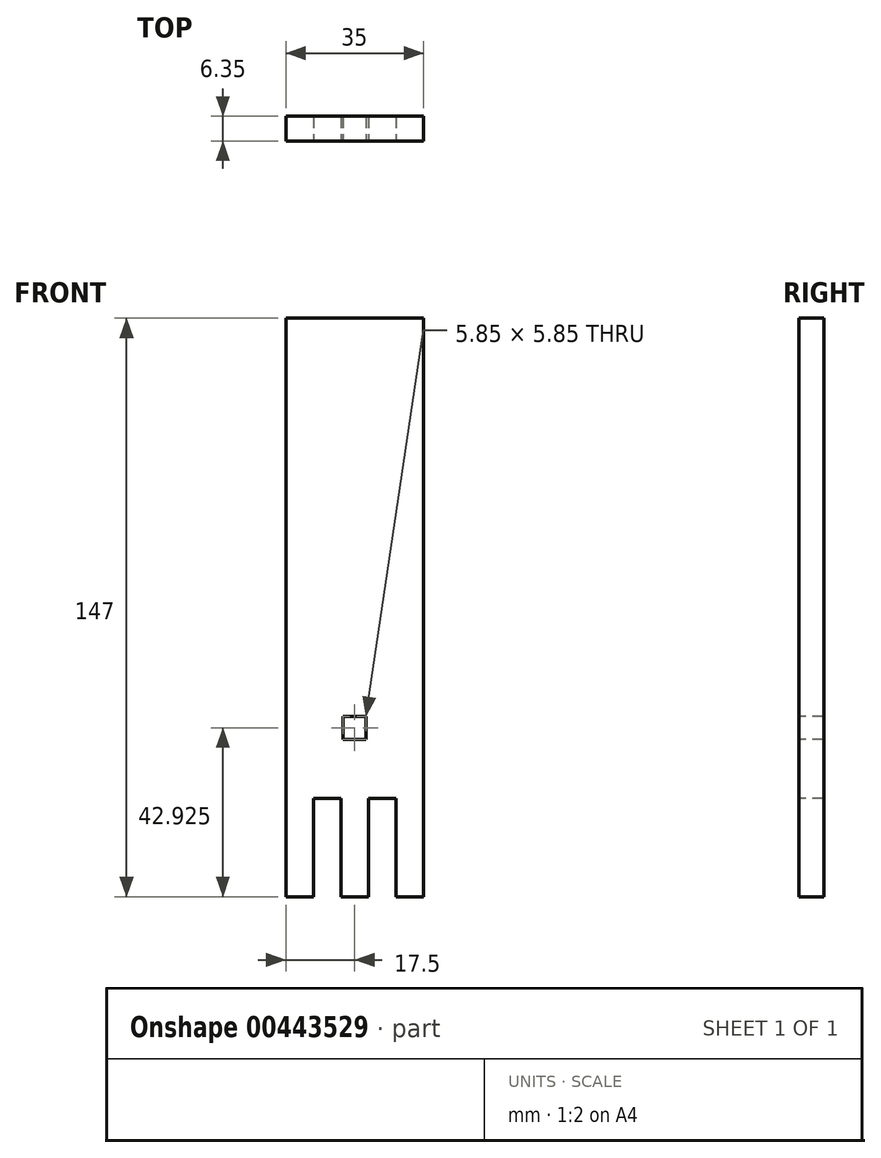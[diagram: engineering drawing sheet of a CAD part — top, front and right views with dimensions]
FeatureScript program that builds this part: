
annotation { "Feature Type Name" : "Feature", "Feature Type Description" : "" }
export const myFeature = defineFeature(function(context is Context, id is Id, definition is map)
    precondition{}
    {
        {
            var Q0;
            Q0=qCreatedBy(makeId("Front.planeOp"),FACE);
            var sketch = newSketch(context, id + "F0", { "sketchPlane" : qUnion([Q0])});
            skLineSegment(sketch, "E0.bottom", {"start": v(0, 0) * mm, "end": v(35, 0) * mm});
            skLineSegment(sketch, "E0.top", {"start": v(0, 122) * mm, "end": v(35, 122) * mm});
            skLineSegment(sketch, "E0.left", {"start": v(0, 0) * mm, "end": v(0, 122) * mm});
            skLineSegment(sketch, "E0.right", {"start": v(35, 0) * mm, "end": v(35, 122) * mm});
            skSolve(sketch);
        }
        {
            var Q0;
            Q0 = qSketchRegion(id + "F0", true);
            extrude(context, id + "F1", {"entities" : qUnion([Q0]), "depth" : 6.35 * mm});
        }
        {
            var Q0;
            Q0=makeQuery(id+"F1.opExtrude","CAP_FACE",FACE,{"disambiguationData":[OSD([sQuery(id+"F0.wireOp",EDGE,"E0.bottom"),sQuery(id+"F0.wireOp",EDGE,"E0.top"),sQuery(id+"F0.wireOp",EDGE,"E0.left"),sQuery(id+"F0.wireOp",EDGE,"E0.right")])],"isStart":false});
            var sketch = newSketch(context, id + "F2", { "sketchPlane" : qUnion([Q0])});
            skLineSegment(sketch, "E1.bottom", {"start": v(0, 0) * mm, "end": v(7, 0) * mm});
            skLineSegment(sketch, "E1.top", {"start": v(0, -25) * mm, "end": v(7, -25) * mm});
            skLineSegment(sketch, "E1.left", {"start": v(0, 0) * mm, "end": v(0, -25) * mm});
            skLineSegment(sketch, "E1.right", {"start": v(7, 0) * mm, "end": v(7, -25) * mm});
            skLineSegment(sketch, "E2.bottom", {"start": v(28, 0) * mm, "end": v(35, 0) * mm});
            skLineSegment(sketch, "E2.top", {"start": v(28, -25) * mm, "end": v(35, -25) * mm});
            skLineSegment(sketch, "E2.left", {"start": v(28, 0) * mm, "end": v(28, -25) * mm});
            skLineSegment(sketch, "E2.right", {"start": v(35, 0) * mm, "end": v(35, -25) * mm});
            skLineSegment(sketch, "E3.bottom", {"start": v(14, 0) * mm, "end": v(21, 0) * mm});
            skLineSegment(sketch, "E3.top", {"start": v(14, -25) * mm, "end": v(21, -25) * mm});
            skLineSegment(sketch, "E3.left", {"start": v(14, 0) * mm, "end": v(14, -25) * mm});
            skLineSegment(sketch, "E3.right", {"start": v(21, 0) * mm, "end": v(21, -25) * mm});
            skSolve(sketch);
        }
        {
            var Q0;
            Q0 = qSketchRegion(id + "F2", true);
            extrude(context, id + "F3", {"entities" : qUnion([Q0]), "operationType" : NewBodyOperationType.ADD, "oppositeDirection" : true, "depth" : 6.35 * mm});
        }
        {
            var Q0;
            Q0=makeQuery(id+"F1.opExtrude","CAP_FACE",FACE,{"disambiguationData":[OSD([sQuery(id+"F0.wireOp",EDGE,"E0.bottom"),sQuery(id+"F0.wireOp",EDGE,"E0.top"),sQuery(id+"F0.wireOp",EDGE,"E0.left"),sQuery(id+"F0.wireOp",EDGE,"E0.right")])],"isStart":false});
            var sketch = newSketch(context, id + "F4", { "sketchPlane" : qUnion([Q0])});
            skLineSegment(sketch, "E4.bottom", {"start": v(14.58, 20.85) * mm, "end": v(20.43, 20.85) * mm});
            skLineSegment(sketch, "E4.top", {"start": v(14.58, 15) * mm, "end": v(20.43, 15) * mm});
            skLineSegment(sketch, "E4.left", {"start": v(14.58, 20.85) * mm, "end": v(14.58, 15) * mm});
            skLineSegment(sketch, "E4.right", {"start": v(20.43, 20.85) * mm, "end": v(20.43, 15) * mm});
            skPoint(sketch, "E5", {"position": v(17.5, 15) * mm});
            skPoint(sketch, "E6", {"position": v(0, 15) * mm});
            skPoint(sketch, "E7", {"position": v(35, 15) * mm});
            skSolve(sketch);
        }
        {
            var Q0;
            Q0 = qSketchRegion(id + "F4", true);
            extrude(context, id + "F5", {"entities" : qUnion([Q0]), "operationType" : NewBodyOperationType.REMOVE, "oppositeDirection" : true, "depth" : 25 * mm});
        }
    });
